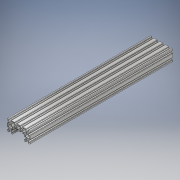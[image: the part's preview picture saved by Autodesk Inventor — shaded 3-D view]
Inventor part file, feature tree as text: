
AUTODESK INVENTOR PART (.ipt)
format: ipt  version: 2019 (Build 230136000, 136)  size: 406,528 bytes
history: native  units: mm
features: extrude x1, sketch x1
ambient origin geometry x8: Origin, YZ Plane, XZ Plane, XY Plane, X Axis, Y Axis, Z Axis, Center Point
bodies: Solid1 (feature_tree)
feature tree (2):
  extrude  "Extrusion1"  [1 undecoded]
  sketch  "Sketch1"  dims[d0=500.0mm d1=0.0mm]
note: 1 required parameter value undecoded (feature->parameter linkage not recoverable at this tier; creation-order binding heuristic only, values carry confidence <= 0.55)
